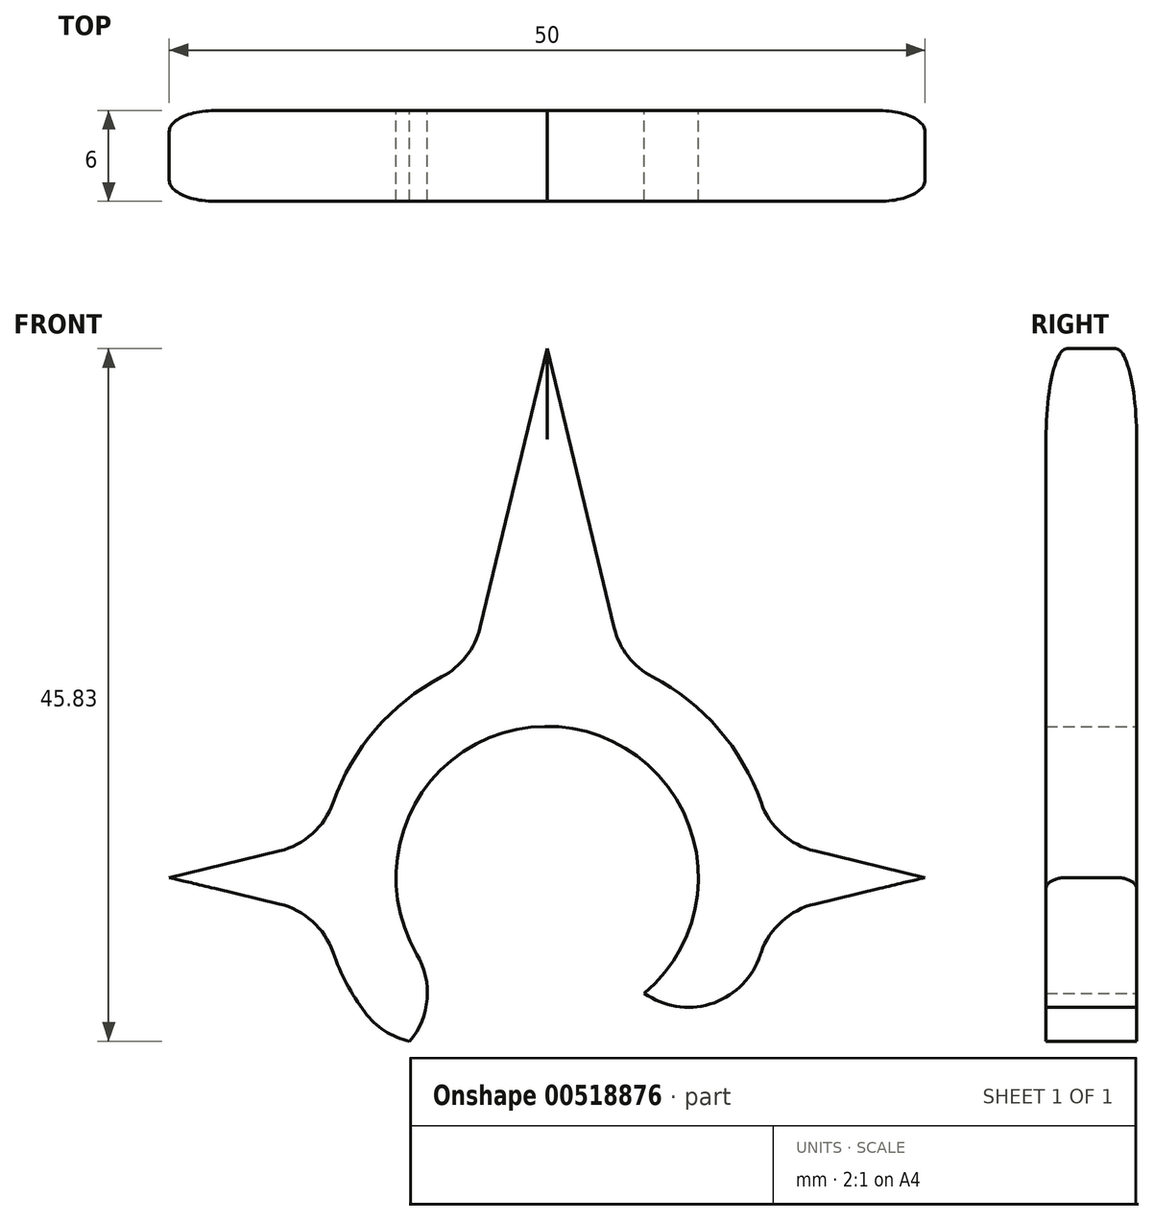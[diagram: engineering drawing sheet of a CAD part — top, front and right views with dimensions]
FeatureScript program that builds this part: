
annotation { "Feature Type Name" : "Feature", "Feature Type Description" : "" }
export const myFeature = defineFeature(function(context is Context, id is Id, definition is map)
    precondition{}
    {
        {
            var Q0;
            Q0=qCreatedBy(makeId("Front.planeOp"),FACE);
            var sketch = newSketch(context, id + "F0", { "sketchPlane" : qUnion([Q0])});
            skArc(sketch, "E0", {"start": v(6.43, -7.66) * mm, "mid": v(0, 10) * mm, "end": v(-6.43, -7.66) * mm});
            skArc(sketch, "E1", {"start": v(9.64, -11.5) * mm, "mid": v(0, 15) * mm, "end": v(-9.64, -11.5) * mm});
            skLineSegment(sketch, "E2", {"start": v(-6.43, -7.66) * mm, "end": v(-9.64, -11.5) * mm});
            skLineSegment(sketch, "E3", {"start": v(6.43, -7.66) * mm, "end": v(9.64, -11.5) * mm});
            skLineSegment(sketch, "E4", {"start": v(5, 14.14) * mm, "end": v(0, 35) * mm});
            skLineSegment(sketch, "E5", {"start": v(0, 35) * mm, "end": v(-5, 14.14) * mm});
            skLineSegment(sketch, "E6", {"start": v(14.8, 2.45) * mm, "end": v(25, 0) * mm});
            skLineSegment(sketch, "E7", {"start": v(25, 0) * mm, "end": v(14.8, -2.45) * mm});
            skLineSegment(sketch, "E8", {"start": v(-14.8, 2.45) * mm, "end": v(-25, 0) * mm});
            skLineSegment(sketch, "E9", {"start": v(-25, 0) * mm, "end": v(-14.8, -2.45) * mm});
            skLineSegment(sketch, "E10", {"start": v(0, 0) * mm, "end": v(0, -26.85) * mm});
            skSolve(sketch);
        }
        {
            var Q0;
            Q0=qSketchRegion(id+"F0",true);
            extrude(context, id + "F1", {"entities" : qUnion([Q0]), "depth" : 6 * mm, "offsetDistance" : 25 * mm});
        }
        {
            var Q0;
            Q0=makeQuery(id+"F1.opExtrude","SWEPT_EDGE",EDGE,{"disambiguationData":[OSD([sQuery(id+"F0.wireOp",EDGE,"E1"),sQuery(id+"F0.wireOp",EDGE,"E5")])]});
            fillet(context, id + "F2", {"entities" : qUnion([Q0]), "radius" : 5 * mm, "tangentPropagation" : true, "allowEdgeOverflow" : false});
        }
        {
            var Q0;
            Q0=makeQuery(id+"F1.opExtrude","SWEPT_EDGE",EDGE,{"disambiguationData":[OSD([sQuery(id+"F0.wireOp",EDGE,"E1"),sQuery(id+"F0.wireOp",EDGE,"E4")])]});
            fillet(context, id + "F3", {"entities" : qUnion([Q0]), "radius" : 5 * mm, "tangentPropagation" : true, "allowEdgeOverflow" : false});
        }
        {
            var Q0;
            Q0=makeQuery(id+"F1.opExtrude","SWEPT_EDGE",EDGE,{"disambiguationData":[OSD([sQuery(id+"F0.wireOp",EDGE,"E0"),sQuery(id+"F0.wireOp",EDGE,"E2")])]});
            fillet(context, id + "F4", {"entities" : qUnion([Q0]), "radius" : 5 * mm, "tangentPropagation" : true, "allowEdgeOverflow" : false});
        }
        {
            var Q0;
            Q0=makeQuery(id+"F1.opExtrude","SWEPT_EDGE",EDGE,{"disambiguationData":[OSD([sQuery(id+"F0.wireOp",EDGE,"E1"),sQuery(id+"F0.wireOp",EDGE,"LFsdBNPY-1jha-I2t7-jOrJ-aUM9VeTVUucY")])]});
            fillet(context, id + "F5", {"entities" : qUnion([Q0]), "radius" : 5 * mm, "tangentPropagation" : true, "allowEdgeOverflow" : false});
        }
        {
            var Q0;
            Q0=makeQuery(id+"F1.opExtrude","CAP_EDGE",EDGE,{"disambiguationData":[OSD([sQuery(id+"F0.wireOp",EDGE,"E4")])],"isStart":false});
            var Q1;
            Q1=makeQuery(id+"F1.opExtrude","CAP_EDGE",EDGE,{"disambiguationData":[OSD([sQuery(id+"F0.wireOp",EDGE,"E5")])],"isStart":false});
            fillet(context, id + "F6", {"entities" : qUnion([Q0, Q1]), "radius" : 1.4 * mm, "tangentPropagation" : true, "allowEdgeOverflow" : false});
        }
        {
            var Q0;
            Q0=makeQuery(id+"F1.opExtrude","CAP_EDGE",EDGE,{"disambiguationData":[OSD([sQuery(id+"F0.wireOp",EDGE,"E4")])],"isStart":true});
            var Q1;
            Q1=makeQuery(id+"F1.opExtrude","CAP_EDGE",EDGE,{"disambiguationData":[OSD([sQuery(id+"F0.wireOp",EDGE,"E5")])],"isStart":true});
            fillet(context, id + "F7", {"entities" : qUnion([Q0, Q1]), "radius" : 1.4 * mm, "tangentPropagation" : true, "allowEdgeOverflow" : false});
        }
    });
